# Revit family: 353_Pipe Inspection TP 200_110
name_source: partatom
category: Plumbing Fixtures
units: mm (PartAtom-declared; Revit-internal decimal feet)

## family parameters
Always vertical = Yes
Cut with Voids When Loaded = No
Part Type = Normal
Room Calculation Point = No
Round Connector Dimension = Use Diameter
Shared = No
Work Plane-Based = No

## types (1)
- Inspection chamber TP 200/110 p/n 086301
    BD3 = 354 mm  [stored 1.16142 ft]
    C1 = 210 mm
    C2 = 190 mm  [stored 0.62336 ft]
    CAT0 = Yes
    CLBTZ = 0 mm  [stored 0 ft]
    CL_Location_5000 = 5000 mm  [stored 16.4042 ft]
    D = 110 mm
    D1 = 110 mm
    Description = Inspection chamber TP 200/110 p/n: 086301
    H1 = 383 mm  [stored 1.25656 ft]
    H1__ve = -383 mm  [stored -1.25656 ft]
    H5 = 12 mm  [stored 0.0393701 ft]
    H5__ve = -12 mm  [stored -0.0393701 ft]
    MC Product Code = Inspection chamber TP 200/110 p/n:086301
    Manufacturer = Pipelife
    QmdConnectorList = 651;D;652;D1
    R = 55 mm  [stored 0.180446 ft]
    URL = http://www.pipelife.fi
    XC = 212 mm  [stored 0.695538 ft]
    XC2 = 424 mm  [stored 1.39108 ft]
    ZC = 318 mm  [stored 1.04331 ft]
    magiPartTypeId = 353
    magiProductFamilyId = Pipe Inspection TP 200/110
    magiProductId = Pipe Inspection TP 200/110

note: [stored X ft] marks values corroborated as IEEE doubles in the binary element streams (Revit-internal decimal feet)

## geometry (parser evidence)
native form markers: Sweep x2
no freeform markers — native parametric forms only
